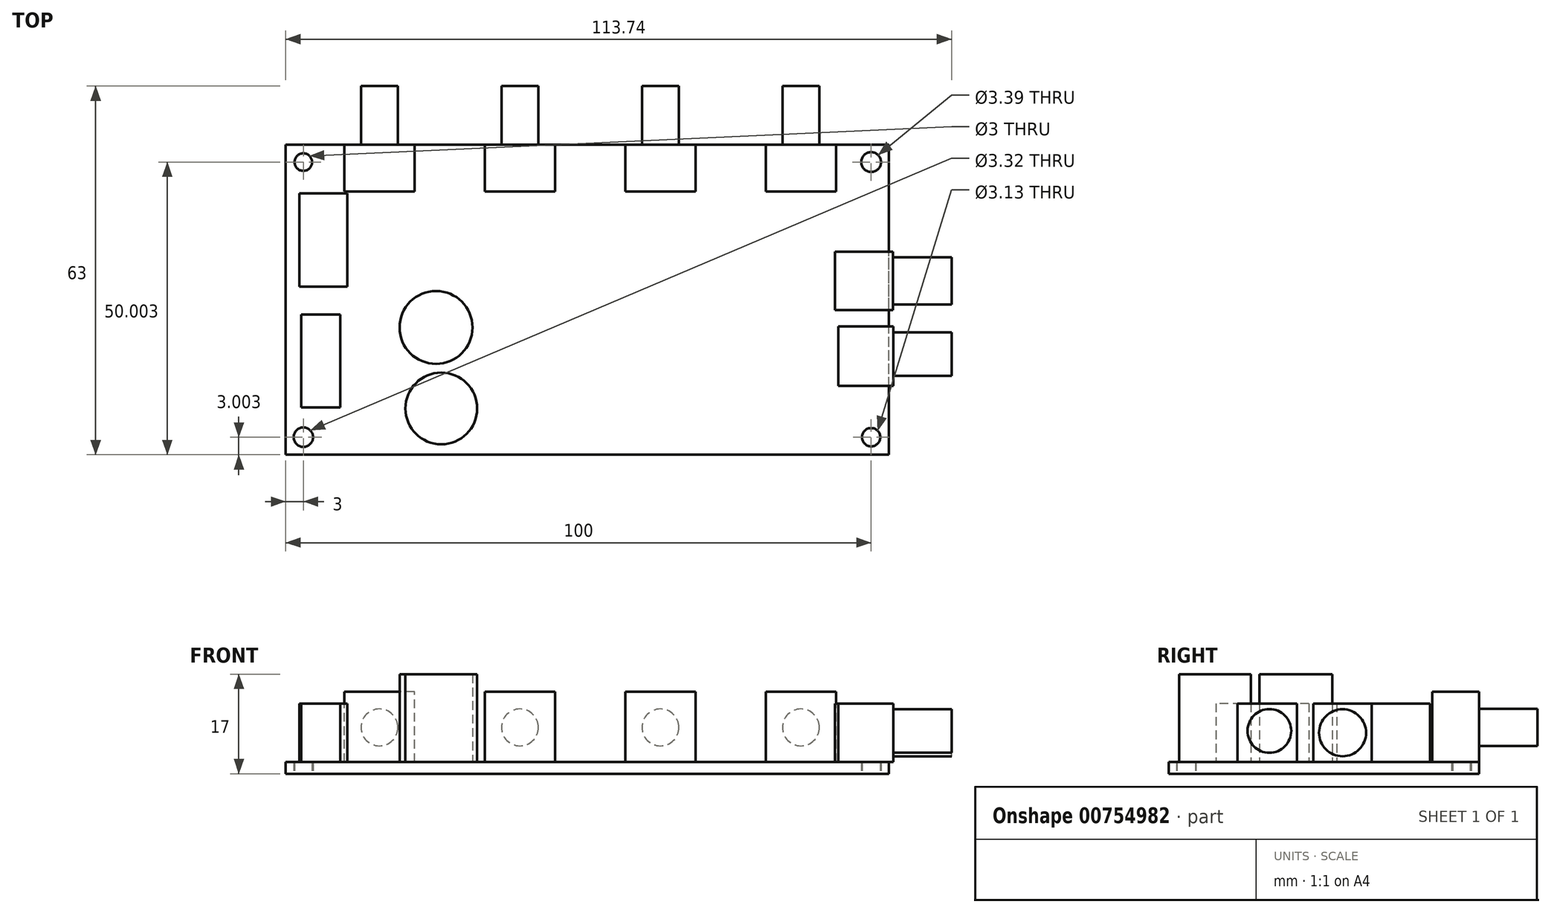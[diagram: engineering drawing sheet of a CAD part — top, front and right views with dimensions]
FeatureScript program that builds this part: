
annotation { "Feature Type Name" : "Feature", "Feature Type Description" : "" }
export const myFeature = defineFeature(function(context is Context, id is Id, definition is map)
    precondition{}
    {
        {
            var Q0;
            Q0=qCreatedBy(makeId("Top.planeOp"),FACE);
            var sketch = newSketch(context, id + "F0", { "sketchPlane" : qUnion([Q0])});
            skLineSegment(sketch, "E0.bottom", {"start": v(-70.02, 26.4) * mm, "end": v(32.98, 26.4) * mm});
            skLineSegment(sketch, "E0.top", {"start": v(-70.02, 79.4) * mm, "end": v(32.98, 79.4) * mm});
            skLineSegment(sketch, "E0.left", {"start": v(-70.02, 26.4) * mm, "end": v(-70.02, 79.4) * mm});
            skLineSegment(sketch, "E0.right", {"start": v(32.98, 26.4) * mm, "end": v(32.98, 79.4) * mm});
            skCircle(sketch, "E1", {"center": v(-67.02, 29.4) * mm, "radius": 1.66 * mm});
            skCircle(sketch, "E2", {"center": v(-67.02, 76.4) * mm, "radius": 1.5 * mm});
            skCircle(sketch, "E3", {"center": v(29.98, 76.4) * mm, "radius": 1.7 * mm});
            skCircle(sketch, "E4", {"center": v(29.98, 29.4) * mm, "radius": 1.56 * mm});
            skLineSegment(sketch, "E5", {"start": v(17.98, 95.79) * mm, "end": v(17.98, 70.5) * mm});
            skSolve(sketch);
        }
        {
            var Q0;
            Q0 = qSketchRegion(id + "F0", true);
            extrude(context, id + "F1", {"entities" : qUnion([Q0]), "depth" : 2 * mm, "offsetDistance" : 25 * mm});
        }
        {
            var Q0;
            Q0=makeQuery(id+"F1.opExtrude","SWEPT_FACE",FACE,{"disambiguationData":[OSD([sQuery(id+"F0.wireOp",EDGE,"E0.top")])]});
            var sketch = newSketch(context, id + "F2", { "sketchPlane" : qUnion([Q0])});
            skLineSegment(sketch, "E6.bottom", {"start": v(-23.98, 2) * mm, "end": v(-11.98, 2) * mm});
            skLineSegment(sketch, "E6.top", {"start": v(-23.98, 14) * mm, "end": v(-11.98, 14) * mm});
            skLineSegment(sketch, "E6.left", {"start": v(-23.98, 2) * mm, "end": v(-23.98, 14) * mm});
            skLineSegment(sketch, "E6.right", {"start": v(-11.98, 2) * mm, "end": v(-11.98, 14) * mm});
            skLineSegment(sketch, "E7.1.0.0", {"start": v(0.02, 2) * mm, "end": v(0.02, 14) * mm});
            skLineSegment(sketch, "E7.1.0.1", {"start": v(0.02, 2) * mm, "end": v(12.02, 2) * mm});
            skLineSegment(sketch, "E7.1.0.2", {"start": v(12.02, 2) * mm, "end": v(12.02, 14) * mm});
            skLineSegment(sketch, "E7.1.0.3", {"start": v(0.02, 14) * mm, "end": v(12.02, 14) * mm});
            skLineSegment(sketch, "E7.2.0.0", {"start": v(24.02, 2) * mm, "end": v(24.02, 14) * mm});
            skLineSegment(sketch, "E7.2.0.1", {"start": v(24.02, 2) * mm, "end": v(36.02, 2) * mm});
            skLineSegment(sketch, "E7.2.0.2", {"start": v(36.02, 2) * mm, "end": v(36.02, 14) * mm});
            skLineSegment(sketch, "E7.2.0.3", {"start": v(24.02, 14) * mm, "end": v(36.02, 14) * mm});
            skLineSegment(sketch, "E7.3.0.0", {"start": v(48.02, 2) * mm, "end": v(48.02, 14) * mm});
            skLineSegment(sketch, "E7.3.0.1", {"start": v(48.02, 2) * mm, "end": v(60.02, 2) * mm});
            skLineSegment(sketch, "E7.3.0.2", {"start": v(60.02, 2) * mm, "end": v(60.02, 14) * mm});
            skLineSegment(sketch, "E7.3.0.3", {"start": v(48.02, 14) * mm, "end": v(60.02, 14) * mm});
            skLineSegment(sketch, "E7.direction1", {"start": v(-23.98, 2) * mm, "end": v(0.02, 2) * mm, "construction": true});
            skSolve(sketch);
        }
        {
            var Q0;
            Q0=makeQuery(id+"F2.imprint","IMPRINT",FACE,{"disambiguationData":[TD([[makeQuery(id+"F2.imprint","IMPRINT",EDGE,{"derivedFrom":sQuery(id+"F2.wireOp",EDGE,"E7.3.0.0")}),-1.0]])]});
            var Q1;
            Q1=makeQuery(id+"F2.imprint","IMPRINT",FACE,{"disambiguationData":[TD([[makeQuery(id+"F2.imprint","IMPRINT",EDGE,{"derivedFrom":sQuery(id+"F2.wireOp",EDGE,"E7.2.0.0")}),-1.0]])]});
            var Q2;
            Q2=makeQuery(id+"F2.imprint","IMPRINT",FACE,{"disambiguationData":[TD([[makeQuery(id+"F2.imprint","IMPRINT",EDGE,{"derivedFrom":sQuery(id+"F2.wireOp",EDGE,"E7.1.0.0")}),-1.0]])]});
            var Q3;
            Q3=makeQuery(id+"F2.imprint","IMPRINT",FACE,{"disambiguationData":[TD([[makeQuery(id+"F2.imprint","IMPRINT",EDGE,{"derivedFrom":sQuery(id+"F2.wireOp",EDGE,"E6.bottom")}),-1.0]])]});
            extrude(context, id + "F3", {"entities" : qUnion([Q0, Q1, Q2, Q3]), "operationType" : NewBodyOperationType.ADD, "oppositeDirection" : true, "depth" : 8 * mm, "offsetDistance" : 25 * mm});
        }
        {
            var Q0;
            Q0=makeQuery(id+"F3.boolean.opBoolean","MERGE",FACE,{"derivedFrom":[makeQuery(id+"F1.opExtrude","SWEPT_FACE",FACE,{"disambiguationData":[OSD([sQuery(id+"F0.wireOp",EDGE,"E0.top")])]}),makeQuery(id+"F3.opExtrude","CAP_FACE",FACE,{"disambiguationData":[OSD([sQuery(id+"F2.wireOp",EDGE,"E6.bottom"),sQuery(id+"F2.wireOp",EDGE,"E6.top"),sQuery(id+"F2.wireOp",EDGE,"E6.left"),sQuery(id+"F2.wireOp",EDGE,"E6.right")])],"isStart":true}),makeQuery(id+"F3.opExtrude","CAP_FACE",FACE,{"disambiguationData":[OSD([sQuery(id+"F2.wireOp",EDGE,"2dda45a7-93f8-4987-82ba-1042c3a75b63.1.0.0"),sQuery(id+"F2.wireOp",EDGE,"2dda45a7-93f8-4987-82ba-1042c3a75b63.1.0.1"),sQuery(id+"F2.wireOp",EDGE,"2dda45a7-93f8-4987-82ba-1042c3a75b63.1.0.2"),sQuery(id+"F2.wireOp",EDGE,"2dda45a7-93f8-4987-82ba-1042c3a75b63.1.0.3")])],"isStart":true}),makeQuery(id+"F3.opExtrude","CAP_FACE",FACE,{"disambiguationData":[OSD([sQuery(id+"F2.wireOp",EDGE,"2dda45a7-93f8-4987-82ba-1042c3a75b63.2.0.0"),sQuery(id+"F2.wireOp",EDGE,"2dda45a7-93f8-4987-82ba-1042c3a75b63.2.0.1"),sQuery(id+"F2.wireOp",EDGE,"2dda45a7-93f8-4987-82ba-1042c3a75b63.2.0.2"),sQuery(id+"F2.wireOp",EDGE,"2dda45a7-93f8-4987-82ba-1042c3a75b63.2.0.3")])],"isStart":true}),makeQuery(id+"F3.opExtrude","CAP_FACE",FACE,{"disambiguationData":[OSD([sQuery(id+"F2.wireOp",EDGE,"2dda45a7-93f8-4987-82ba-1042c3a75b63.3.0.0"),sQuery(id+"F2.wireOp",EDGE,"2dda45a7-93f8-4987-82ba-1042c3a75b63.3.0.1"),sQuery(id+"F2.wireOp",EDGE,"2dda45a7-93f8-4987-82ba-1042c3a75b63.3.0.2"),sQuery(id+"F2.wireOp",EDGE,"2dda45a7-93f8-4987-82ba-1042c3a75b63.3.0.3")])],"isStart":true})]});
            var sketch = newSketch(context, id + "F4", { "sketchPlane" : qUnion([Q0])});
            skCircle(sketch, "E8", {"center": v(-17.98, 7.91) * mm, "radius": 3.15 * mm});
            skPoint(sketch, "E8.centerSnap0", {"position": v(-17.98, 14) * mm});
            skCircle(sketch, "E9.1.0.0", {"center": v(6.02, 7.91) * mm, "radius": 3.15 * mm});
            skCircle(sketch, "E9.2.0.0", {"center": v(30.02, 7.91) * mm, "radius": 3.15 * mm});
            skCircle(sketch, "E9.3.0.0", {"center": v(54.02, 7.91) * mm, "radius": 3.15 * mm});
            skLineSegment(sketch, "E9.direction1", {"start": v(-17.98, 7.91) * mm, "end": v(6.02, 7.91) * mm, "construction": true});
            skSolve(sketch);
        }
        {
            var Q0;
            Q0 = qSketchRegion(id + "F4", true);
            extrude(context, id + "F5", {"entities" : qUnion([Q0]), "operationType" : NewBodyOperationType.ADD, "depth" : 10 * mm, "offsetDistance" : 25 * mm});
        }
        {
            var Q0;
            Q0=makeQuery(id+"F1.opExtrude","CAP_FACE",FACE,{"disambiguationData":[OSD([sQuery(id+"F0.wireOp",EDGE,"E0.bottom"),sQuery(id+"F0.wireOp",EDGE,"E0.top"),sQuery(id+"F0.wireOp",EDGE,"E0.left"),sQuery(id+"F0.wireOp",EDGE,"E0.right"),sQuery(id+"F0.wireOp",EDGE,"E1"),sQuery(id+"F0.wireOp",EDGE,"E2"),sQuery(id+"F0.wireOp",EDGE,"E3"),sQuery(id+"F0.wireOp",EDGE,"E4")])],"isStart":false});
            var sketch = newSketch(context, id + "F6", { "sketchPlane" : qUnion([Q0])});
            skLineSegment(sketch, "E10.bottom", {"start": v(-67.7, 71.05) * mm, "end": v(-59.52, 71.05) * mm});
            skLineSegment(sketch, "E10.top", {"start": v(-67.7, 55.13) * mm, "end": v(-59.52, 55.13) * mm});
            skLineSegment(sketch, "E10.left", {"start": v(-67.7, 71.05) * mm, "end": v(-67.7, 55.13) * mm});
            skLineSegment(sketch, "E10.right", {"start": v(-59.52, 71.05) * mm, "end": v(-59.52, 55.13) * mm});
            skLineSegment(sketch, "E11.bottom", {"start": v(-67.4, 50.37) * mm, "end": v(-60.71, 50.37) * mm});
            skLineSegment(sketch, "E11.top", {"start": v(-67.4, 34.45) * mm, "end": v(-60.71, 34.45) * mm});
            skLineSegment(sketch, "E11.left", {"start": v(-67.4, 50.37) * mm, "end": v(-67.4, 34.45) * mm});
            skLineSegment(sketch, "E11.right", {"start": v(-60.71, 50.37) * mm, "end": v(-60.71, 34.45) * mm});
            skLineSegment(sketch, "E12.bottom", {"start": v(23.78, 61.08) * mm, "end": v(33.72, 61.08) * mm});
            skLineSegment(sketch, "E12.top", {"start": v(23.78, 51.11) * mm, "end": v(33.72, 51.11) * mm});
            skLineSegment(sketch, "E12.left", {"start": v(23.78, 61.08) * mm, "end": v(23.78, 51.11) * mm});
            skLineSegment(sketch, "E12.right", {"start": v(33.72, 61.08) * mm, "end": v(33.72, 51.11) * mm});
            skLineSegment(sketch, "E13.bottom", {"start": v(24.38, 48.29) * mm, "end": v(33.76, 48.29) * mm});
            skLineSegment(sketch, "E13.top", {"start": v(24.38, 38.17) * mm, "end": v(33.76, 38.17) * mm});
            skLineSegment(sketch, "E13.left", {"start": v(24.38, 48.29) * mm, "end": v(24.38, 38.17) * mm});
            skLineSegment(sketch, "E13.right", {"start": v(33.76, 48.29) * mm, "end": v(33.76, 38.17) * mm});
            skSolve(sketch);
        }
        {
            var Q0;
            Q0 = qSketchRegion(id + "F6", true);
            extrude(context, id + "F7", {"entities" : qUnion([Q0]), "operationType" : NewBodyOperationType.ADD, "depth" : 10 * mm, "offsetDistance" : 25 * mm});
        }
        {
            var Q0;
            Q0=makeQuery(id+"F1.opExtrude","CAP_FACE",FACE,{"disambiguationData":[OSD([sQuery(id+"F0.wireOp",EDGE,"E0.bottom"),sQuery(id+"F0.wireOp",EDGE,"E0.top"),sQuery(id+"F0.wireOp",EDGE,"E0.left"),sQuery(id+"F0.wireOp",EDGE,"E0.right"),sQuery(id+"F0.wireOp",EDGE,"E1"),sQuery(id+"F0.wireOp",EDGE,"E2"),sQuery(id+"F0.wireOp",EDGE,"E3"),sQuery(id+"F0.wireOp",EDGE,"E4")])],"isStart":false});
            var sketch = newSketch(context, id + "F8", { "sketchPlane" : qUnion([Q0])});
            skCircle(sketch, "E14", {"center": v(-44.35, 48.14) * mm, "radius": 6.23 * mm});
            skCircle(sketch, "E15", {"center": v(-43.46, 34.3) * mm, "radius": 6.12 * mm});
            skSolve(sketch);
        }
        {
            var Q0;
            Q0 = qSketchRegion(id + "F8", true);
            extrude(context, id + "F9", {"entities" : qUnion([Q0]), "operationType" : NewBodyOperationType.ADD, "depth" : 15 * mm, "offsetDistance" : 25 * mm});
        }
        {
            var Q0;
            Q0=makeQuery(id+"F7.opExtrude","SWEPT_FACE",FACE,{"disambiguationData":[OSD([sQuery(id+"F6.wireOp",EDGE,"E12.right")])]});
            var sketch = newSketch(context, id + "F10", { "sketchPlane" : qUnion([Q0])});
            skCircle(sketch, "E16", {"center": v(56.1, 7) * mm, "radius": 4.02 * mm});
            skPoint(sketch, "E16.centerSnap0", {"position": v(51.11, 7) * mm});
            skPoint(sketch, "E16.centerSnap1", {"position": v(56.1, 2) * mm});
            skCircle(sketch, "E17", {"center": v(43.6, 7.31) * mm, "radius": 3.73 * mm});
            skSolve(sketch);
        }
        {
            var Q0;
            Q0 = qSketchRegion(id + "F10", true);
            extrude(context, id + "F11", {"entities" : qUnion([Q0]), "operationType" : NewBodyOperationType.ADD, "depth" : 10 * mm, "offsetDistance" : 25 * mm});
        }
    });
